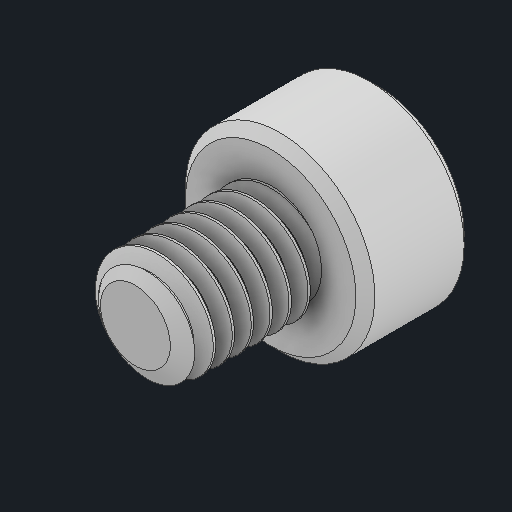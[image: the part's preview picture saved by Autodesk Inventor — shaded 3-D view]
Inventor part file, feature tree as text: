
AUTODESK INVENTOR PART (.ipt)
format: ipt  version: 2023 (Build 270158000, 158)  size: 349,696 bytes
history: native  units: in
note: dims shown in document units (in); Inventor stores cm internally (conversion verified against a paired STEP export)
features: chamfer x1
ambient origin geometry x8: Origin, YZ Plane, XZ Plane, XY Plane, X Axis, Y Axis, Z Axis, Center Point
bodies: Solid1 (feature_tree)
feature tree (1):
  chamfer  "Chamfer1"  [1 undecoded]
note: 1 required parameter value undecoded (feature->parameter linkage not recoverable at this tier; creation-order binding heuristic only, values carry confidence <= 0.55)
